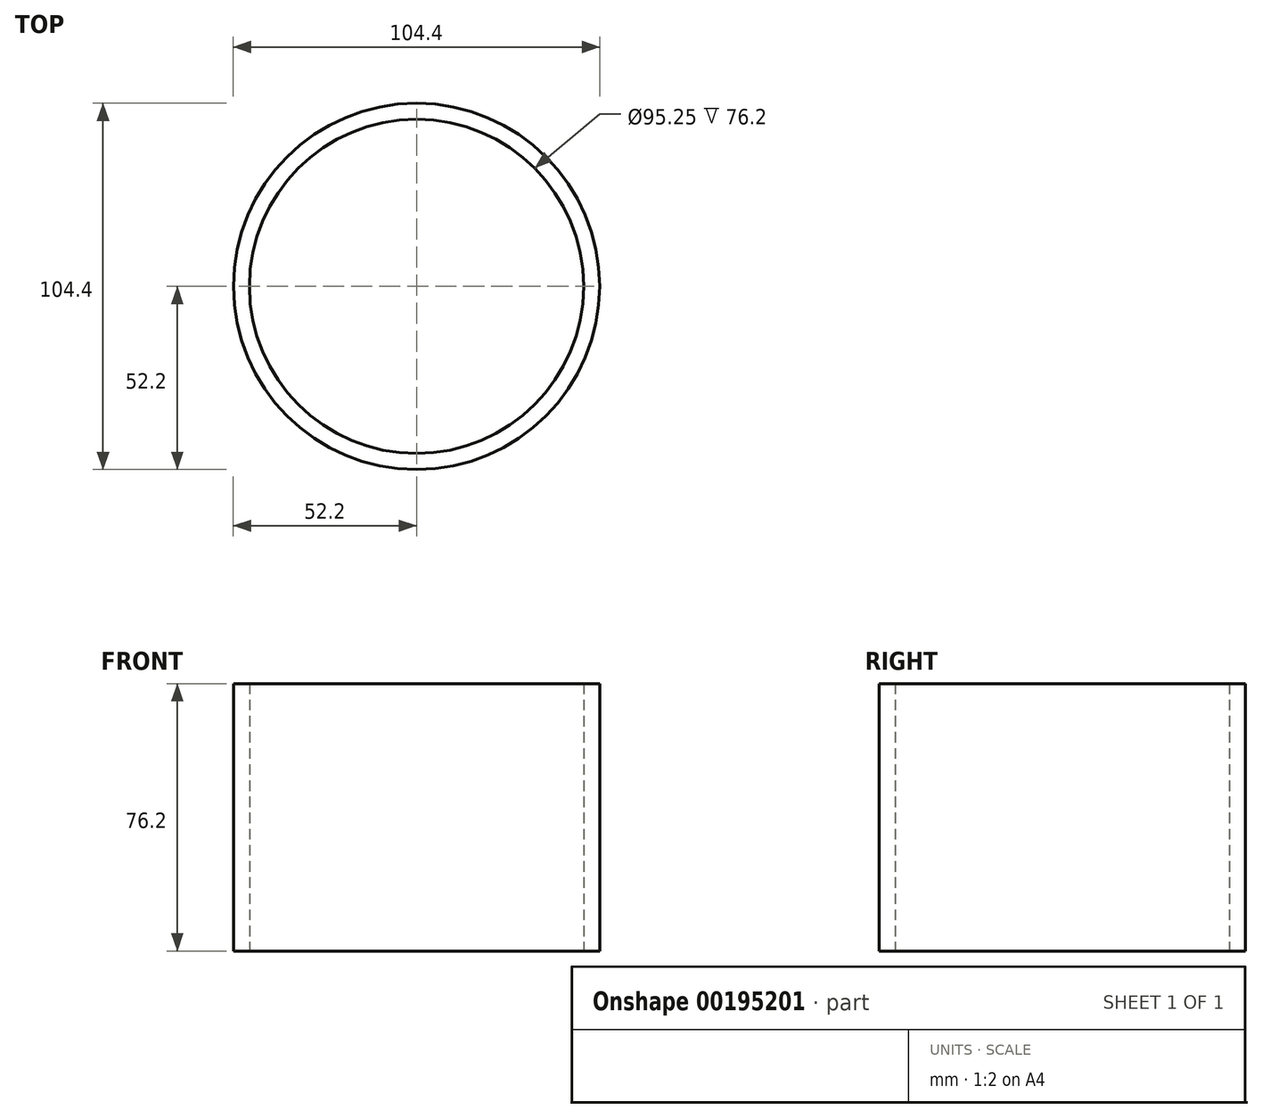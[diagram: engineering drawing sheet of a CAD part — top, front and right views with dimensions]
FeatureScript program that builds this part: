
annotation { "Feature Type Name" : "Feature", "Feature Type Description" : "" }
export const myFeature = defineFeature(function(context is Context, id is Id, definition is map)
    precondition{}
    {
        {
            var Q0;
            Q0=qCreatedBy(makeId("Top.planeOp"),FACE);
            var sketch = newSketch(context, id + "F0", { "sketchPlane" : qUnion([Q0])});
            skCircle(sketch, "E0", {"center": v(0, 0) * mm, "radius": 52.2 * mm});
            skCircle(sketch, "E1", {"center": v(0, 0) * mm, "radius": 47.63 * mm});
            skSolve(sketch);
        }
        {
            var Q0;
            Q0 = qSketchRegion(id + "F0", true);
            extrude(context, id + "F1", {"entities" : qUnion([Q0]), "depth" : 76.2 * mm});
        }
    });
